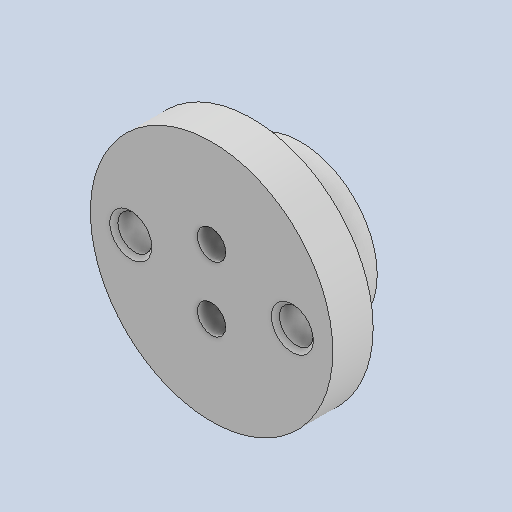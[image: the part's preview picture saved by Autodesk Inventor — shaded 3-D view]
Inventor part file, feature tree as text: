
AUTODESK INVENTOR PART (.ipt)
format: ipt  version: 2023 (Build 270158000, 158)  size: 171,008 bytes
history: native  units: in
note: dims shown in document units (in); Inventor stores cm internally (conversion verified against a paired STEP export)
features: extrude x4, sketch x4, chamfer x1
ambient origin geometry x8: Origin, YZ Plane, XZ Plane, XY Plane, X Axis, Y Axis, Z Axis, Center Point
bodies: Solid1 (feature_tree)
feature tree (9):
  extrude  "Extrusion1"  Depth=0.4331in TaperAngle=0.0deg
  extrude  "Extrusion4"  Depth=0.1378in
  extrude  "Extrusion2"  Depth=0.1575in
  extrude  "Extrusion3"  Depth=0.1969in
  chamfer  "Chamfer1"  Distance=0.1654in
  sketch  "Sketch2"  dims[d0=0.748in d1=0.4331in d2=0.0in]
  sketch  "Sketch3"  dims[d3=0.1378in d4=0.1378in]
  sketch  "Sketch4"  dims[d5=0.315in d6=0.1575in]
  sketch  "Sketch5"  dims[d7=0.0in d8=0.0in d9=0.1654in d10=0.1654in d11=0.7874in d12=0.1969in d13=0.0in d14=0.0197in d15=0.0787in d16=45.0deg d17=1.1811in d18=0.1969in d19=0.0in]
